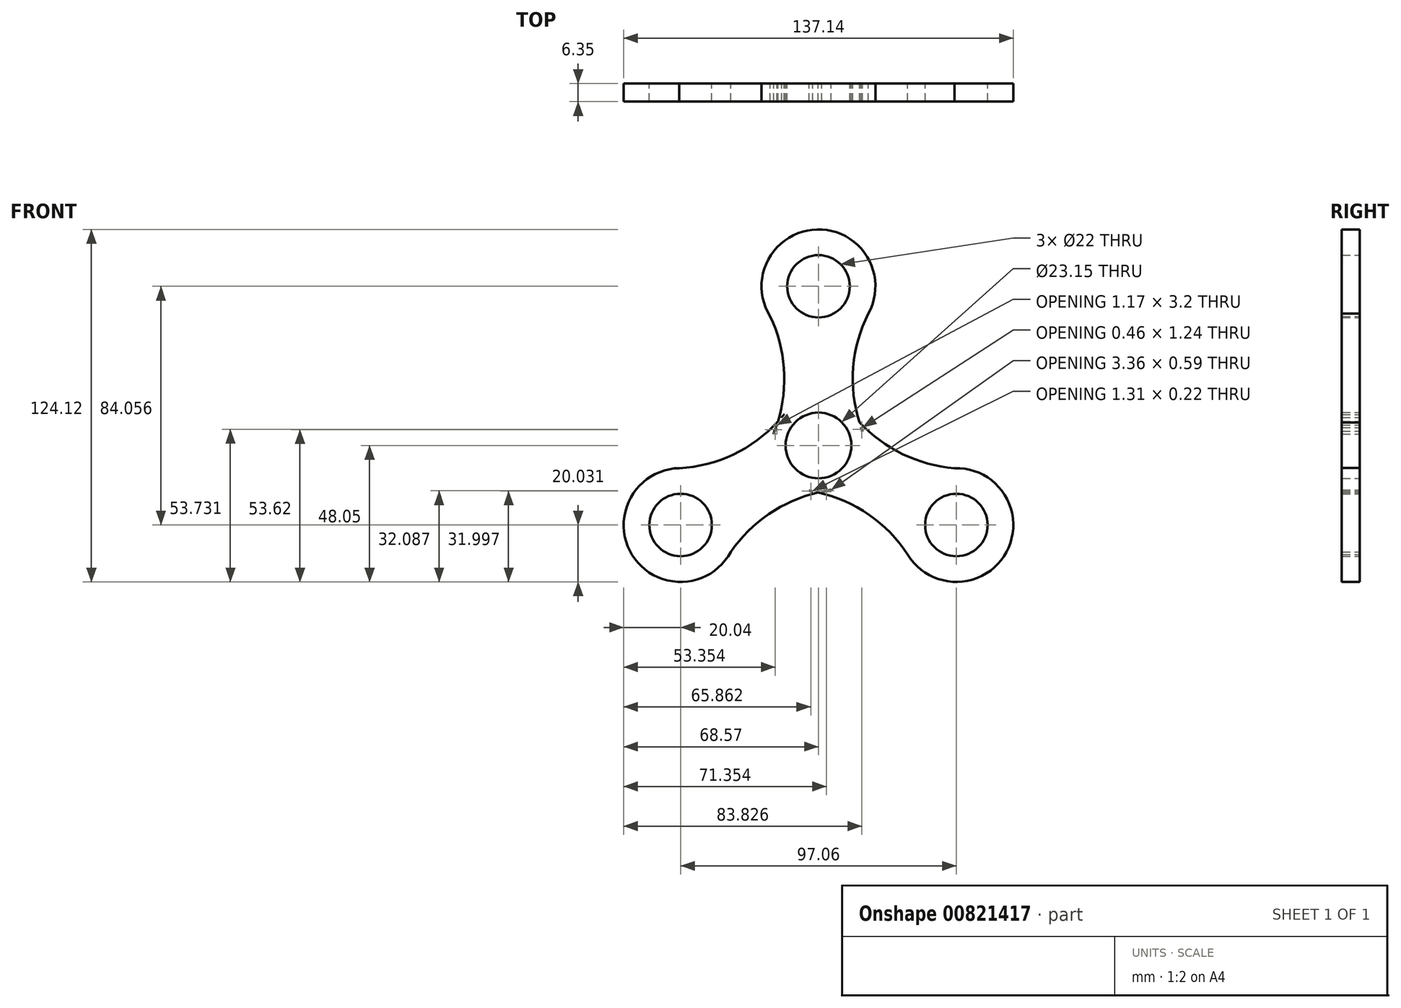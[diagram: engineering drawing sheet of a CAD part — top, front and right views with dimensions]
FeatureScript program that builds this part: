
annotation { "Feature Type Name" : "Feature", "Feature Type Description" : "" }
export const myFeature = defineFeature(function(context is Context, id is Id, definition is map)
    precondition{}
    {
        {
            var Q0;
            Q0=qCreatedBy(makeId("Front.planeOp"),FACE);
            var sketch = newSketch(context, id + "F0", { "sketchPlane" : qUnion([Q0])});
            skCircle(sketch, "E0", {"center": v(0, 0) * mm, "radius": 11.57 * mm});
            skCircle(sketch, "E1", {"center": v(0, 56.04) * mm, "radius": 11 * mm});
            skArc(sketch, "E2", {"start": v(17.57, 46.4) * mm, "mid": v(-0.55, 76.07) * mm, "end": v(-17.01, 45.46) * mm});
            skArc(sketch, "E3", {"start": v(-12.13, 10.88) * mm, "mid": v(-14.39, 7.65) * mm, "end": v(-15.8, 3.97) * mm});
            skArc(sketch, "E4", {"start": v(17.57, 46.4) * mm, "mid": v(12.12, 25.95) * mm, "end": v(15.49, 5.06) * mm});
            skArc(sketch, "E5", {"start": v(-15.8, 3.97) * mm, "mid": v(-12.14, 26.48) * mm, "end": v(-18.52, 48.39) * mm});
            skCircle(sketch, "E6.1.0", {"center": v(-48.53, -28.02) * mm, "radius": 11 * mm});
            skArc(sketch, "E6.1.1", {"start": v(-48.97, -7.99) * mm, "mid": v(-65.6, -38.5) * mm, "end": v(-30.86, -37.46) * mm});
            skArc(sketch, "E6.1.2", {"start": v(-48.97, -7.99) * mm, "mid": v(-28.54, -2.48) * mm, "end": v(-12.13, 10.88) * mm});
            skArc(sketch, "E6.1.3", {"start": v(4.46, -15.67) * mm, "mid": v(-16.87, -23.75) * mm, "end": v(-32.65, -40.23) * mm});
            skArc(sketch, "E6.1.4", {"start": v(-12.13, 10.88) * mm, "mid": v(-13.5, 9.11) * mm, "end": v(-14.63, 7.17) * mm});
            skCircle(sketch, "E6.2.0", {"center": v(48.53, -28.02) * mm, "radius": 11 * mm});
            skArc(sketch, "E6.2.1", {"start": v(31.4, -38.42) * mm, "mid": v(66.15, -37.56) * mm, "end": v(47.87, -8) * mm});
            skArc(sketch, "E6.2.2", {"start": v(31.4, -38.42) * mm, "mid": v(16.42, -23.48) * mm, "end": v(-3.36, -15.94) * mm});
            skArc(sketch, "E6.2.3", {"start": v(11.34, 11.7) * mm, "mid": v(29, -2.73) * mm, "end": v(51.16, -8.16) * mm});
            skArc(sketch, "E6.2.4", {"start": v(-12.13, 10.88) * mm, "mid": v(-12.56, 10.38) * mm, "end": v(-12.97, 9.86) * mm});
            skArc(sketch, "E7.trimOffspring", {"start": v(-2.05, -16.16) * mm, "mid": v(-0.48, -16.29) * mm, "end": v(1.1, -16.26) * mm});
            skArc(sketch, "E8.trimOffspring", {"start": v(-3.36, -15.94) * mm, "mid": v(0.57, -16.28) * mm, "end": v(4.46, -15.67) * mm});
            skArc(sketch, "E9.trimOffspring", {"start": v(15.49, 5.06) * mm, "mid": v(14.65, 7.14) * mm, "end": v(13.53, 9.08) * mm});
            skArc(sketch, "E10.trimOffspring", {"start": v(-3.36, -15.94) * mm, "mid": v(-1.14, -16.25) * mm, "end": v(1.1, -16.26) * mm});
            skSolve(sketch);
        }
        {
            var Q0;
            Q0 = qSketchRegion(id + "F0", true);
            extrude(context, id + "F1", {"entities" : qUnion([Q0]), "depth" : 6.35 * mm, "offsetDistance" : 25.4 * mm});
        }
    });
